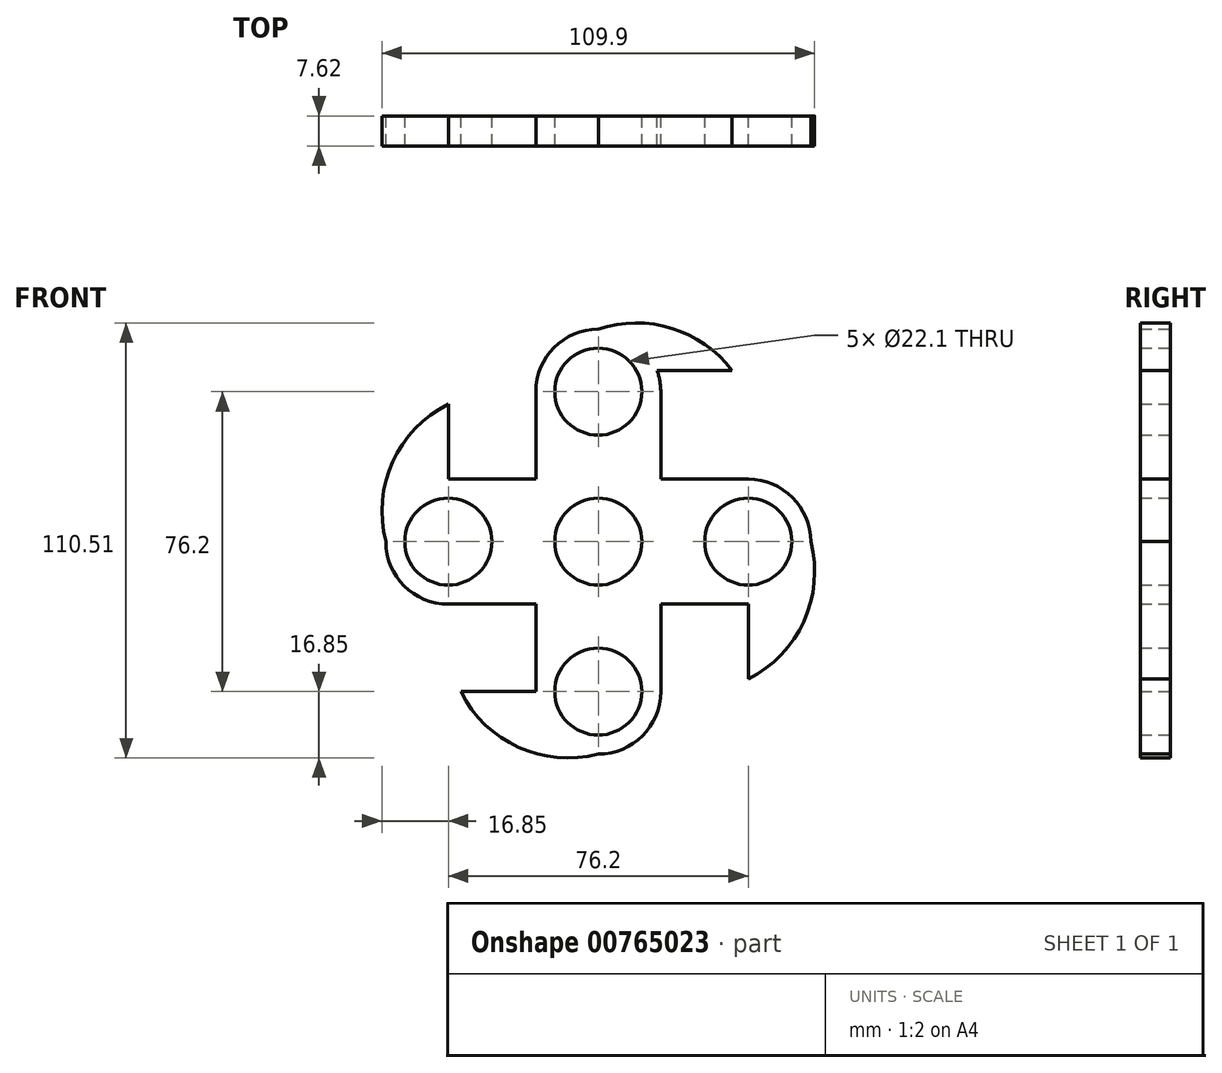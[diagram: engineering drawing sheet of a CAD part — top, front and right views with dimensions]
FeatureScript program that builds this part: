
annotation { "Feature Type Name" : "Feature", "Feature Type Description" : "" }
export const myFeature = defineFeature(function(context is Context, id is Id, definition is map)
    precondition{}
    {
        {
            var Q0;
            Q0=qCreatedBy(makeId("Front.planeOp"),FACE);
            var sketch = newSketch(context, id + "F0", { "sketchPlane" : qUnion([Q0])});
            skCircle(sketch, "E0", {"center": v(0, 0) * mm, "radius": 11.05 * mm});
            skCircle(sketch, "E1", {"center": v(0, 38.1) * mm, "radius": 11.05 * mm});
            skCircle(sketch, "E2", {"center": v(-38.1, 0) * mm, "radius": 11.05 * mm});
            skCircle(sketch, "E3", {"center": v(38.1, 0) * mm, "radius": 11.05 * mm});
            skCircle(sketch, "E4", {"center": v(0, -38.1) * mm, "radius": 11.05 * mm});
            skCircle(sketch, "E5", {"center": v(0, 38.1) * mm, "radius": 15.88 * mm});
            skCircle(sketch, "E6", {"center": v(-38.1, 0) * mm, "radius": 15.88 * mm});
            skCircle(sketch, "E7", {"center": v(38.1, 0) * mm, "radius": 15.88 * mm});
            skCircle(sketch, "E8", {"center": v(0, -38.1) * mm, "radius": 15.88 * mm});
            skLineSegment(sketch, "E9", {"start": v(-15.88, 0) * mm, "end": v(-15.88, 38.1) * mm});
            skLineSegment(sketch, "E10", {"start": v(15.88, 0) * mm, "end": v(15.88, 38.1) * mm});
            skLineSegment(sketch, "E11", {"start": v(0, 15.88) * mm, "end": v(-38.1, 15.88) * mm});
            skLineSegment(sketch, "E12", {"start": v(0, -15.87) * mm, "end": v(-38.1, -15.87) * mm});
            skLineSegment(sketch, "E13", {"start": v(0, 15.88) * mm, "end": v(38.1, 15.88) * mm});
            skLineSegment(sketch, "E14", {"start": v(0, -15.87) * mm, "end": v(38.1, -15.87) * mm});
            skLineSegment(sketch, "E15", {"start": v(-15.88, 0) * mm, "end": v(-15.88, -38.1) * mm});
            skLineSegment(sketch, "E16", {"start": v(15.87, 12.7) * mm, "end": v(15.88, -38.1) * mm});
            skArc(sketch, "E17", {"start": v(-38.1, 34.93) * mm, "mid": v(-52.22, 20.27) * mm, "end": v(-53.97, 0) * mm});
            skLineSegment(sketch, "E18", {"start": v(-38.1, 34.93) * mm, "end": v(-38.1, 15.88) * mm});
            skArc(sketch, "E19", {"start": v(-34.93, -38.1) * mm, "mid": v(-20.27, -52.22) * mm, "end": v(0, -53.98) * mm});
            skLineSegment(sketch, "E20", {"start": v(-34.92, -38.1) * mm, "end": v(-15.87, -38.1) * mm});
            skArc(sketch, "E21", {"start": v(38.1, -34.92) * mm, "mid": v(52.22, -20.27) * mm, "end": v(53.98, 0) * mm});
            skLineSegment(sketch, "E22", {"start": v(38.1, -34.92) * mm, "end": v(38.1, -15.87) * mm});
            skArc(sketch, "E23", {"start": v(33.97, 43.51) * mm, "mid": v(18.67, 54.2) * mm, "end": v(0, 53.97) * mm});
            skLineSegment(sketch, "E24", {"start": v(33.97, 43.51) * mm, "end": v(14.92, 43.51) * mm});
            skSolve(sketch);
        }
        {
            var Q0;
            Q0 = qSketchRegion(id + "F0", true);
            extrude(context, id + "F1", {"entities" : qUnion([Q0]), "depth" : 7.62 * mm, "offsetDistance" : 25.4 * mm});
        }
    });
